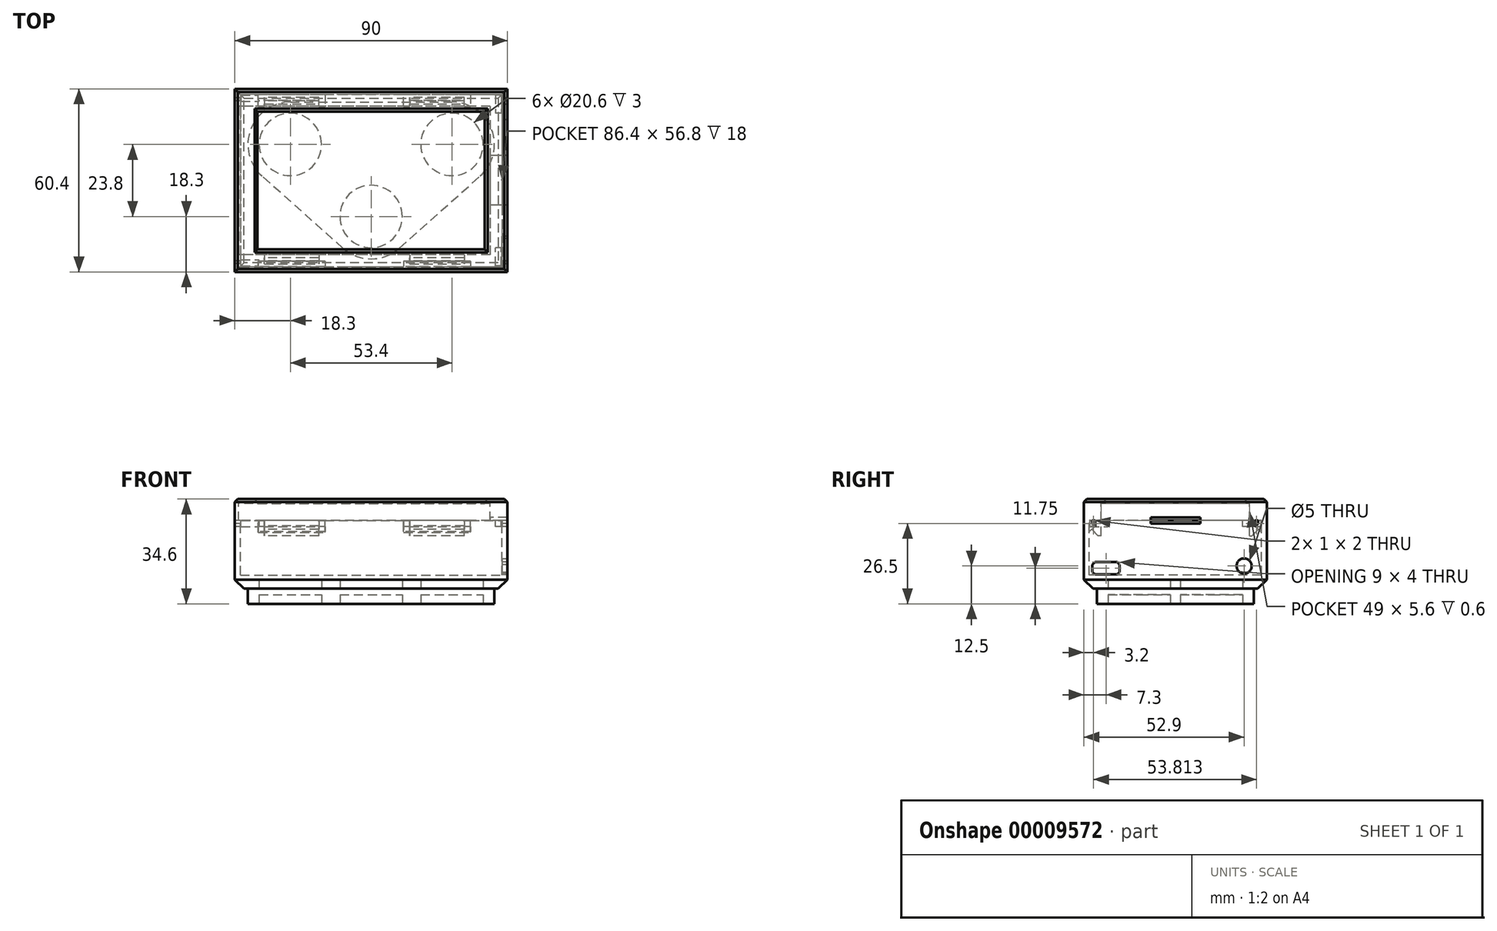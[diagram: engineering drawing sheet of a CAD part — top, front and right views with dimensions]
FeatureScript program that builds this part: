
annotation { "Feature Type Name" : "Feature", "Feature Type Description" : "" }
export const myFeature = defineFeature(function(context is Context, id is Id, definition is map)
    precondition{}
    {
        {
            var Q0;
            Q0=qCreatedBy(makeId("Top.planeOp"),FACE);
            var sketch = newSketch(context, id + "F0", { "sketchPlane" : qUnion([Q0])});
            skLineSegment(sketch, "E0.bottom", {"start": v(-82.5, 48.4) * mm, "end": v(0, 48.4) * mm});
            skLineSegment(sketch, "E0.top", {"start": v(-82.5, 0) * mm, "end": v(0, 0) * mm});
            skLineSegment(sketch, "E0.left", {"start": v(-82.5, 48.4) * mm, "end": v(-82.5, 0) * mm});
            skLineSegment(sketch, "E0.right", {"start": v(0, 48.4) * mm, "end": v(0, 0) * mm});
            skLineSegment(sketch, "E1", {"start": v(-78, 48.4) * mm, "end": v(-78, 0) * mm, "construction": true});
            skLineSegment(sketch, "E2", {"start": v(-78, 48.4) * mm, "end": v(0, 0) * mm, "construction": true});
            skLineSegment(sketch, "E3", {"start": v(0, 48.4) * mm, "end": v(-78, 0) * mm, "construction": true});
            skPoint(sketch, "E4", {"position": v(-39, 24.2) * mm});
            skSolve(sketch);
        }
        {
            var Q0;
            Q0=qCreatedBy(makeId("Top.planeOp"),FACE);
            var sketch = newSketch(context, id + "F1", { "sketchPlane" : qUnion([Q0])});
            skLineSegment(sketch, "E5.bottom", {"start": v(6, 54.4) * mm, "end": v(-84, 54.4) * mm});
            skLineSegment(sketch, "E5.top", {"start": v(6, -6) * mm, "end": v(-84, -6) * mm});
            skLineSegment(sketch, "E5.left", {"start": v(6, 54.4) * mm, "end": v(6, -6) * mm});
            skLineSegment(sketch, "E5.right", {"start": v(-84, 54.4) * mm, "end": v(-84, -6) * mm});
            skPoint(sketch, "E6", {"position": v(-39, 54.4) * mm});
            skPoint(sketch, "E7", {"position": v(6, 24.2) * mm});
            skLineSegment(sketch, "E8.bottom", {"start": v(-76.5, 46.9) * mm, "end": v(-1.5, 46.9) * mm});
            skLineSegment(sketch, "E8.top", {"start": v(-76.5, 1.5) * mm, "end": v(-1.5, 1.5) * mm});
            skLineSegment(sketch, "E8.left", {"start": v(-76.5, 46.9) * mm, "end": v(-76.5, 1.5) * mm});
            skLineSegment(sketch, "E8.right", {"start": v(-1.5, 46.9) * mm, "end": v(-1.5, 1.5) * mm});
            skSolve(sketch);
        }
        {
            var Q0;
            Q0 = qSketchRegion(id + "F1", true);
            extrude(context, id + "F2", {"entities" : qUnion([Q0]), "depth" : 1.5 * mm});
        }
        {
            var Q0;
            Q0=makeQuery(id+"F2.opExtrude","CAP_EDGE",EDGE,{"disambiguationData":[OSD([sQuery(id+"F1.wireOp",EDGE,"E8.bottom")])],"isStart":false});
            var Q1;
            Q1=makeQuery(id+"F2.opExtrude","CAP_EDGE",EDGE,{"disambiguationData":[OSD([sQuery(id+"F1.wireOp",EDGE,"E8.left")])],"isStart":false});
            var Q2;
            Q2=makeQuery(id+"F2.opExtrude","CAP_EDGE",EDGE,{"disambiguationData":[OSD([sQuery(id+"F1.wireOp",EDGE,"E8.top")])],"isStart":false});
            var Q3;
            Q3=makeQuery(id+"F2.opExtrude","CAP_EDGE",EDGE,{"disambiguationData":[OSD([sQuery(id+"F1.wireOp",EDGE,"E8.right")])],"isStart":false});
            var Q4;
            Q4=makeQuery(id+"F2.opExtrude","CAP_EDGE",EDGE,{"disambiguationData":[OSD([sQuery(id+"F1.wireOp",EDGE,"E5.right")])],"isStart":false});
            var Q5;
            Q5=makeQuery(id+"F2.opExtrude","CAP_EDGE",EDGE,{"disambiguationData":[OSD([sQuery(id+"F1.wireOp",EDGE,"E5.top")])],"isStart":false});
            var Q6;
            Q6=makeQuery(id+"F2.opExtrude","CAP_EDGE",EDGE,{"disambiguationData":[OSD([sQuery(id+"F1.wireOp",EDGE,"E5.left")])],"isStart":false});
            var Q7;
            Q7=makeQuery(id+"F2.opExtrude","CAP_EDGE",EDGE,{"disambiguationData":[OSD([sQuery(id+"F1.wireOp",EDGE,"E5.bottom")])],"isStart":false});
            chamfer(context, id + "F3", {"entities" : qUnion([Q0, Q1, Q2, Q3, Q4, Q5, Q6, Q7]), "width" : 1 * mm, "tangentPropagation" : true});
        }
        {
            var Q0;
            Q0=makeQuery(id+"F2.opExtrude","CAP_FACE",FACE,{"disambiguationData":[OSD([sQuery(id+"F1.wireOp",EDGE,"E5.bottom"),sQuery(id+"F1.wireOp",EDGE,"E5.top"),sQuery(id+"F1.wireOp",EDGE,"E5.left"),sQuery(id+"F1.wireOp",EDGE,"E5.right"),sQuery(id+"F1.wireOp",EDGE,"E8.bottom"),sQuery(id+"F1.wireOp",EDGE,"E8.top"),sQuery(id+"F1.wireOp",EDGE,"E8.left"),sQuery(id+"F1.wireOp",EDGE,"E8.right")])],"isStart":true});
            var sketch = newSketch(context, id + "F4", { "sketchPlane" : qUnion([Q0])});
            skLineSegment(sketch, "E9", {"start": v(-84, 6) * mm, "end": v(-84, -54.4) * mm});
            skLineSegment(sketch, "E10", {"start": v(-84, -54.4) * mm, "end": v(6, -54.4) * mm});
            skLineSegment(sketch, "E11", {"start": v(6, -54.4) * mm, "end": v(6, 6) * mm});
            skLineSegment(sketch, "E12", {"start": v(6, 6) * mm, "end": v(-84, 6) * mm});
            skLineSegment(sketch, "E13.bottom", {"start": v(0.3, -48.7) * mm, "end": v(-82.8, -48.7) * mm});
            skLineSegment(sketch, "E13.top", {"start": v(0.3, 0.3) * mm, "end": v(-82.8, 0.3) * mm});
            skLineSegment(sketch, "E13.left", {"start": v(0.3, -48.7) * mm, "end": v(0.3, 0.3) * mm});
            skLineSegment(sketch, "E13.right", {"start": v(-82.8, -48.7) * mm, "end": v(-82.8, 0.3) * mm});
            skSolve(sketch);
        }
        {
            var Q0;
            Q0 = qSketchRegion(id + "F4", true);
            extrude(context, id + "F5", {"entities" : qUnion([Q0]), "operationType" : NewBodyOperationType.ADD, "depth" : 5.6 * mm});
        }
        {
            var Q0;
            Q0=makeQuery(id+"F5.opExtrude","CAP_FACE",FACE,{"disambiguationData":[OSD([sQuery(id+"F4.wireOp",EDGE,"E9"),sQuery(id+"F4.wireOp",EDGE,"E10"),sQuery(id+"F4.wireOp",EDGE,"E11"),sQuery(id+"F4.wireOp",EDGE,"E12"),sQuery(id+"F4.wireOp",EDGE,"E13.bottom"),sQuery(id+"F4.wireOp",EDGE,"E13.top"),sQuery(id+"F4.wireOp",EDGE,"E13.left"),sQuery(id+"F4.wireOp",EDGE,"E13.right")])],"isStart":false});
            var sketch = newSketch(context, id + "F6", { "sketchPlane" : qUnion([Q0])});
            skLineSegment(sketch, "E14.bottom", {"start": v(6, -16) * mm, "end": v(0.3, -16) * mm});
            skLineSegment(sketch, "E14.top", {"start": v(6, -32.4) * mm, "end": v(0.3, -32.4) * mm});
            skLineSegment(sketch, "E14.left", {"start": v(6, -16) * mm, "end": v(6, -32.4) * mm});
            skLineSegment(sketch, "E14.right", {"start": v(0.3, -16) * mm, "end": v(0.3, -32.4) * mm});
            skSolve(sketch);
        }
        {
            var Q0;
            Q0 = qSketchRegion(id + "F6", true);
            extrude(context, id + "F7", {"entities" : qUnion([Q0]), "operationType" : NewBodyOperationType.REMOVE, "oppositeDirection" : true, "depth" : 0.4 * mm});
        }
        {
            var Q0;
            Q0=makeQuery(id+"F5.opExtrude","CAP_FACE",FACE,{"disambiguationData":[OSD([sQuery(id+"F4.wireOp",EDGE,"E9"),sQuery(id+"F4.wireOp",EDGE,"E10"),sQuery(id+"F4.wireOp",EDGE,"E11"),sQuery(id+"F4.wireOp",EDGE,"E12"),sQuery(id+"F4.wireOp",EDGE,"E13.bottom"),sQuery(id+"F4.wireOp",EDGE,"E13.top"),sQuery(id+"F4.wireOp",EDGE,"E13.left"),sQuery(id+"F4.wireOp",EDGE,"E13.right")])],"isStart":false});
            var sketch = newSketch(context, id + "F8", { "sketchPlane" : qUnion([Q0])});
            skLineSegment(sketch, "E15", {"start": v(-84, 6) * mm, "end": v(-84, -54.4) * mm});
            skLineSegment(sketch, "E16", {"start": v(-84, -54.4) * mm, "end": v(6, -54.4) * mm});
            skLineSegment(sketch, "E17", {"start": v(6, -54.4) * mm, "end": v(6, 6) * mm});
            skLineSegment(sketch, "E18", {"start": v(6, 6) * mm, "end": v(-84, 6) * mm});
            skSolve(sketch);
        }
        {
            var Q0;
            Q0 = qSketchRegion(id + "F8", true);
            extrude(context, id + "F9", {"entities" : qUnion([Q0]), "depth" : 22.5 * mm});
        }
        {
            var Q0;
            Q0=makeQuery(id+"F9.opExtrude","CAP_FACE",FACE,{"disambiguationData":[OSD([sQuery(id+"F8.wireOp",EDGE,"E15"),sQuery(id+"F8.wireOp",EDGE,"E16"),sQuery(id+"F8.wireOp",EDGE,"E17"),sQuery(id+"F8.wireOp",EDGE,"E18")])],"isStart":true});
            var sketch = newSketch(context, id + "F10", { "sketchPlane" : qUnion([Q0])});
            skLineSegment(sketch, "E19.bottom", {"start": v(6, 32.4) * mm, "end": v(0.3, 32.4) * mm});
            skLineSegment(sketch, "E19.top", {"start": v(6, 16) * mm, "end": v(0.3, 16) * mm});
            skLineSegment(sketch, "E19.left", {"start": v(6, 32.4) * mm, "end": v(6, 16) * mm});
            skLineSegment(sketch, "E19.right", {"start": v(0.3, 32.4) * mm, "end": v(0.3, 16) * mm});
            skSolve(sketch);
        }
        {
            var Q0;
            Q0 = qSketchRegion(id + "F10", true);
            extrude(context, id + "F11", {"entities" : qUnion([Q0]), "operationType" : NewBodyOperationType.REMOVE, "endBound" : BoundingType.SYMMETRIC, "oppositeDirection" : true, "depth" : 2 * mm});
        }
        {
            var Q0;
            Q0=makeQuery(id+"F9.opExtrude","SWEPT_FACE",FACE,{"disambiguationData":[OSD([sQuery(id+"F8.wireOp",EDGE,"E17")])]});
            var sketch = newSketch(context, id + "F12", { "sketchPlane" : qUnion([Q0])});
            skCircle(sketch, "E20", {"center": v(46.9, -20.6) * mm, "radius": 2.5 * mm});
            skSolve(sketch);
        }
        {
            var Q0;
            Q0 = qSketchRegion(id + "F12", true);
            extrude(context, id + "F13", {"entities" : qUnion([Q0]), "operationType" : NewBodyOperationType.REMOVE, "oppositeDirection" : true, "depth" : 20 * mm});
        }
        {
            var Q0;
            Q0=makeQuery(id+"F9.opExtrude","CAP_FACE",FACE,{"disambiguationData":[OSD([sQuery(id+"F8.wireOp",EDGE,"E15"),sQuery(id+"F8.wireOp",EDGE,"E16"),sQuery(id+"F8.wireOp",EDGE,"E17"),sQuery(id+"F8.wireOp",EDGE,"E18")])],"isStart":true});
            var sketch = newSketch(context, id + "F14", { "sketchPlane" : qUnion([Q0])});
            skLineSegment(sketch, "E21.bottom", {"start": v(-82.2, 52.6) * mm, "end": v(4.2, 52.6) * mm});
            skLineSegment(sketch, "E21.top", {"start": v(-82.2, -4.2) * mm, "end": v(4.2, -4.2) * mm});
            skLineSegment(sketch, "E21.left", {"start": v(-82.2, 52.6) * mm, "end": v(-82.2, -4.2) * mm});
            skLineSegment(sketch, "E21.right", {"start": v(4.2, 52.6) * mm, "end": v(4.2, -4.2) * mm});
            skSolve(sketch);
        }
        {
            var Q0;
            Q0 = qSketchRegion(id + "F14", true);
            extrude(context, id + "F15", {"entities" : qUnion([Q0]), "operationType" : NewBodyOperationType.REMOVE, "oppositeDirection" : true, "depth" : 18 * mm});
        }
        {
            var Q0;
            Q0=makeQuery(id+"F15.boolean.opBoolean","COPY",FACE,{"derivedFrom":makeQuery(id+"F15.opExtrude","SWEPT_FACE",FACE,{"disambiguationData":[OSD([sQuery(id+"F14.wireOp",EDGE,"E21.right")])]})});
            var sketch = newSketch(context, id + "F16", { "sketchPlane" : qUnion([Q0])});
            skLineSegment(sketch, "E22.bottom", {"start": v(3.2, -19.35) * mm, "end": v(-5.8, -19.35) * mm});
            skLineSegment(sketch, "E22.top", {"start": v(3.2, -23.35) * mm, "end": v(-5.8, -23.35) * mm});
            skLineSegment(sketch, "E22.left", {"start": v(3.2, -19.35) * mm, "end": v(3.2, -23.35) * mm});
            skLineSegment(sketch, "E22.right", {"start": v(-5.8, -19.35) * mm, "end": v(-5.8, -23.35) * mm});
            skPoint(sketch, "E23", {"position": v(-1.3, -19.35) * mm});
            skPoint(sketch, "E24", {"position": v(-5.8, -21.35) * mm});
            skSolve(sketch);
        }
        {
            var Q0;
            Q0 = qSketchRegion(id + "F16", true);
            var Q1;
            Q1=makeQuery(id+"F9.opExtrude","SWEPT_FACE",FACE,{"disambiguationData":[OSD([sQuery(id+"F8.wireOp",EDGE,"E17")])]});
            extrude(context, id + "F17", {"entities" : qUnion([Q0]), "operationType" : NewBodyOperationType.REMOVE, "endBound" : BoundingType.UP_TO_SURFACE, "oppositeDirection" : true, "endBoundEntityFace" : qUnion([Q1]), "depth" : 25 * mm});
        }
        {
            var Q0;
            Q0=makeQuery(id+"F17.boolean.opBoolean","COPY",EDGE,{"derivedFrom":makeQuery(id+"F17.opExtrude","SWEPT_EDGE",EDGE,{"disambiguationData":[OSD([sQuery(id+"F16.wireOp",EDGE,"E22.top"),sQuery(id+"F16.wireOp",EDGE,"E22.left")])]})});
            var Q1;
            Q1=makeQuery(id+"F17.boolean.opBoolean","COPY",EDGE,{"derivedFrom":makeQuery(id+"F17.opExtrude","SWEPT_EDGE",EDGE,{"disambiguationData":[OSD([sQuery(id+"F16.wireOp",EDGE,"E22.bottom"),sQuery(id+"F16.wireOp",EDGE,"E22.left")])]})});
            var Q2;
            Q2=makeQuery(id+"F17.boolean.opBoolean","COPY",EDGE,{"derivedFrom":makeQuery(id+"F17.opExtrude","SWEPT_EDGE",EDGE,{"disambiguationData":[OSD([sQuery(id+"F16.wireOp",EDGE,"E22.bottom"),sQuery(id+"F16.wireOp",EDGE,"E22.right")])]})});
            var Q3;
            Q3=makeQuery(id+"F17.boolean.opBoolean","COPY",EDGE,{"derivedFrom":makeQuery(id+"F17.opExtrude","SWEPT_EDGE",EDGE,{"disambiguationData":[OSD([sQuery(id+"F16.wireOp",EDGE,"E22.top"),sQuery(id+"F16.wireOp",EDGE,"E22.right")])]})});
            chamfer(context, id + "F18", {"entities" : qUnion([Q0, Q1, Q2, Q3]), "width" : 0.8 * mm, "tangentPropagation" : true});
        }
        {
            var Q0;
            Q0=makeQuery(id+"F9.opExtrude","CAP_FACE",FACE,{"disambiguationData":[OSD([sQuery(id+"F8.wireOp",EDGE,"E15"),sQuery(id+"F8.wireOp",EDGE,"E16"),sQuery(id+"F8.wireOp",EDGE,"E17"),sQuery(id+"F8.wireOp",EDGE,"E18")])],"isStart":false});
            var sketch = newSketch(context, id + "F19", { "sketchPlane" : qUnion([Q0])});
            skCircle(sketch, "E25", {"center": v(-12.3, -36.1) * mm, "radius": 10.3 * mm});
            skCircle(sketch, "E26", {"center": v(-65.7, -36.1) * mm, "radius": 10.3 * mm});
            skCircle(sketch, "E27", {"center": v(-39, -12.3) * mm, "radius": 10.3 * mm});
            skLineSegment(sketch, "E28", {"start": v(-12.3, -46.4) * mm, "end": v(-65.7, -46.4) * mm, "construction": true});
            skLineSegment(sketch, "E29", {"start": v(-72.55, -28.41) * mm, "end": v(-45.85, -4.61) * mm, "construction": true});
            skLineSegment(sketch, "E30", {"start": v(-32.15, -4.61) * mm, "end": v(-5.45, -28.41) * mm, "construction": true});
            skPoint(sketch, "E31", {"position": v(-39, -46.4) * mm});
            skPoint(sketch, "E32", {"position": v(-39, -54.4) * mm});
            skSolve(sketch);
        }
        {
            var Q0;
            Q0 = qSketchRegion(id + "F19", true);
            extrude(context, id + "F20", {"entities" : qUnion([Q0]), "operationType" : NewBodyOperationType.REMOVE, "oppositeDirection" : true, "depth" : 3 * mm});
        }
        {
            var Q0;
            Q0=makeQuery(id+"F9.opExtrude","CAP_EDGE",EDGE,{"disambiguationData":[OSD([sQuery(id+"F8.wireOp",EDGE,"E17")])],"isStart":false});
            var Q1;
            Q1=makeQuery(id+"F9.opExtrude","CAP_EDGE",EDGE,{"disambiguationData":[OSD([sQuery(id+"F8.wireOp",EDGE,"E16")])],"isStart":false});
            var Q2;
            Q2=makeQuery(id+"F9.opExtrude","CAP_EDGE",EDGE,{"disambiguationData":[OSD([sQuery(id+"F8.wireOp",EDGE,"E15")])],"isStart":false});
            var Q3;
            Q3=makeQuery(id+"F9.opExtrude","CAP_EDGE",EDGE,{"disambiguationData":[OSD([sQuery(id+"F8.wireOp",EDGE,"E18")])],"isStart":false});
            chamfer(context, id + "F21", {"entities" : qUnion([Q0, Q1, Q2, Q3]), "width" : 3 * mm, "tangentPropagation" : true});
        }
        {
            var Q0;
            Q0=makeQuery(id+"F5.opExtrude","CAP_FACE",FACE,{"disambiguationData":[OSD([sQuery(id+"F4.wireOp",EDGE,"E9"),sQuery(id+"F4.wireOp",EDGE,"E10"),sQuery(id+"F4.wireOp",EDGE,"E11"),sQuery(id+"F4.wireOp",EDGE,"E12"),sQuery(id+"F4.wireOp",EDGE,"E13.bottom"),sQuery(id+"F4.wireOp",EDGE,"E13.top"),sQuery(id+"F4.wireOp",EDGE,"E13.left"),sQuery(id+"F4.wireOp",EDGE,"E13.right")])],"isStart":false});
            var sketch = newSketch(context, id + "F22", { "sketchPlane" : qUnion([Q0])});
            skLineSegment(sketch, "E33.bottom", {"start": v(-74.25, 0.3) * mm, "end": v(-56.25, 0.3) * mm});
            skLineSegment(sketch, "E33.top", {"start": v(-74.25, 3.3) * mm, "end": v(-56.25, 3.3) * mm});
            skLineSegment(sketch, "E33.left", {"start": v(-74.25, 0.3) * mm, "end": v(-74.25, 3.3) * mm});
            skLineSegment(sketch, "E33.right", {"start": v(-56.25, 0.3) * mm, "end": v(-56.25, 3.3) * mm});
            skLineSegment(sketch, "E34.bottom", {"start": v(-26.25, 0.3) * mm, "end": v(-8.25, 0.3) * mm});
            skLineSegment(sketch, "E34.top", {"start": v(-26.25, 3.3) * mm, "end": v(-8.25, 3.3) * mm});
            skLineSegment(sketch, "E34.left", {"start": v(-26.25, 0.3) * mm, "end": v(-26.25, 3.3) * mm});
            skLineSegment(sketch, "E34.right", {"start": v(-8.25, 0.3) * mm, "end": v(-8.25, 3.3) * mm});
            skLineSegment(sketch, "E35.bottom", {"start": v(-74.25, -48.7) * mm, "end": v(-56.25, -48.7) * mm});
            skLineSegment(sketch, "E35.top", {"start": v(-74.25, -51.51) * mm, "end": v(-56.25, -51.51) * mm});
            skLineSegment(sketch, "E35.left", {"start": v(-74.25, -48.7) * mm, "end": v(-74.25, -51.51) * mm});
            skLineSegment(sketch, "E35.right", {"start": v(-56.25, -48.7) * mm, "end": v(-56.25, -51.51) * mm});
            skLineSegment(sketch, "E36.bottom", {"start": v(-26.25, -48.7) * mm, "end": v(-8.25, -48.7) * mm});
            skLineSegment(sketch, "E36.top", {"start": v(-26.25, -51.51) * mm, "end": v(-8.25, -51.51) * mm});
            skLineSegment(sketch, "E36.left", {"start": v(-26.25, -48.7) * mm, "end": v(-26.25, -51.51) * mm});
            skLineSegment(sketch, "E36.right", {"start": v(-8.25, -48.7) * mm, "end": v(-8.25, -51.51) * mm});
            skPoint(sketch, "E37", {"position": v(-41.25, 0.3) * mm});
            skSolve(sketch);
        }
        {
            var Q0;
            Q0 = qSketchRegion(id + "F22", true);
            extrude(context, id + "F23", {"entities" : qUnion([Q0]), "operationType" : NewBodyOperationType.ADD, "depth" : 5 * mm});
        }
        {
            var Q0;
            Q0=makeQuery(id+"F5.boolean.opBoolean","MERGE",FACE,{"derivedFrom":[makeQuery(id+"F2.opExtrude","SWEPT_FACE",FACE,{"disambiguationData":[OSD([sQuery(id+"F1.wireOp",EDGE,"E5.right")])]}),makeQuery(id+"F5.opExtrude","SWEPT_FACE",FACE,{"disambiguationData":[OSD([sQuery(id+"F4.wireOp",EDGE,"E9")])]})]});
            var sketch = newSketch(context, id + "F24", { "sketchPlane" : qUnion([Q0])});
            skLineSegment(sketch, "E38.bottom", {"start": v(-51.51, -5.6) * mm, "end": v(-50.51, -5.6) * mm});
            skLineSegment(sketch, "E38.top", {"start": v(-51.51, -7.6) * mm, "end": v(-50.51, -7.6) * mm});
            skLineSegment(sketch, "E38.left", {"start": v(-51.51, -5.6) * mm, "end": v(-51.51, -7.6) * mm});
            skLineSegment(sketch, "E38.right", {"start": v(-50.51, -5.6) * mm, "end": v(-50.51, -7.6) * mm});
            skLineSegment(sketch, "E39.bottom", {"start": v(3.3, -5.6) * mm, "end": v(2.3, -5.6) * mm});
            skLineSegment(sketch, "E39.top", {"start": v(3.3, -7.6) * mm, "end": v(2.3, -7.6) * mm});
            skLineSegment(sketch, "E39.left", {"start": v(3.3, -5.6) * mm, "end": v(3.3, -7.6) * mm});
            skLineSegment(sketch, "E39.right", {"start": v(2.3, -5.6) * mm, "end": v(2.3, -7.6) * mm});
            skSolve(sketch);
        }
        {
            var Q0;
            Q0 = qSketchRegion(id + "F24", true);
            extrude(context, id + "F25", {"entities" : qUnion([Q0]), "operationType" : NewBodyOperationType.REMOVE, "endBound" : BoundingType.THROUGH_ALL, "oppositeDirection" : true, "depth" : 25 * mm});
        }
        {
            var Q0;
            Q0=makeQuery(id+"F23.opExtrude","CAP_EDGE",EDGE,{"disambiguationData":[OSD([sQuery(id+"F22.wireOp",EDGE,"E36.top")])],"isStart":false});
            var Q1;
            Q1=makeQuery(id+"F23.opExtrude","CAP_EDGE",EDGE,{"disambiguationData":[OSD([sQuery(id+"F22.wireOp",EDGE,"E35.top")])],"isStart":false});
            var Q2;
            Q2=makeQuery(id+"F23.opExtrude","CAP_EDGE",EDGE,{"disambiguationData":[OSD([sQuery(id+"F22.wireOp",EDGE,"E33.top")])],"isStart":false});
            var Q3;
            Q3=makeQuery(id+"F23.opExtrude","CAP_EDGE",EDGE,{"disambiguationData":[OSD([sQuery(id+"F22.wireOp",EDGE,"E34.top")])],"isStart":false});
            chamfer(context, id + "F26", {"entities" : qUnion([Q0, Q1, Q2, Q3]), "width" : 2 * mm, "tangentPropagation" : true});
        }
        {
            var Q0;
            Q0=makeQuery(id+"F25.boolean.opBoolean","COPY",EDGE,{"disambiguationData":[OD(1.0)],"derivedFrom":makeQuery(id+"F25.opExtrude","SWEPT_EDGE",EDGE,{"disambiguationData":[OSD([sQuery(id+"F24.wireOp",EDGE,"E39.top"),sQuery(id+"F24.wireOp",EDGE,"E39.left")])]})});
            var Q1;
            Q1=makeQuery(id+"F25.boolean.opBoolean","COPY",EDGE,{"disambiguationData":[OD(0.0)],"derivedFrom":makeQuery(id+"F25.opExtrude","SWEPT_EDGE",EDGE,{"disambiguationData":[OSD([sQuery(id+"F24.wireOp",EDGE,"E39.top"),sQuery(id+"F24.wireOp",EDGE,"E39.left")])]})});
            var Q2;
            Q2=makeQuery(id+"F25.boolean.opBoolean","COPY",EDGE,{"disambiguationData":[OD(1.0)],"derivedFrom":makeQuery(id+"F25.opExtrude","SWEPT_EDGE",EDGE,{"disambiguationData":[OSD([sQuery(id+"F24.wireOp",EDGE,"E38.top"),sQuery(id+"F24.wireOp",EDGE,"E38.left")])]})});
            var Q3;
            Q3=makeQuery(id+"F25.boolean.opBoolean","COPY",EDGE,{"disambiguationData":[OD(0.0)],"derivedFrom":makeQuery(id+"F25.opExtrude","SWEPT_EDGE",EDGE,{"disambiguationData":[OSD([sQuery(id+"F24.wireOp",EDGE,"E38.top"),sQuery(id+"F24.wireOp",EDGE,"E38.left")])]})});
            chamfer(context, id + "F27", {"entities" : qUnion([Q0, Q1, Q2, Q3]), "width" : 1 * mm, "tangentPropagation" : true});
        }
        {
            var Q0;
            Q0=makeQuery(id+"F22.imprint","IMPRINT",FACE,{"disambiguationData":[TD([[makeQuery(id+"F22.imprint","IMPRINT",EDGE,{"derivedFrom":sQuery(id+"F22.wireOp",EDGE,"E33.top")}),1.0]])]});
            var sketch = newSketch(context, id + "F28", { "sketchPlane" : qUnion([Q0])});
            skLineSegment(sketch, "E40.bottom", {"start": v(-76.25, -52.6) * mm, "end": v(-54.25, -52.6) * mm});
            skLineSegment(sketch, "E40.top", {"start": v(-76.25, -50.71) * mm, "end": v(-54.25, -50.71) * mm});
            skLineSegment(sketch, "E40.left", {"start": v(-76.25, -50.71) * mm, "end": v(-76.25, -52.6) * mm});
            skLineSegment(sketch, "E40.right", {"start": v(-54.25, -50.71) * mm, "end": v(-54.25, -52.6) * mm});
            skLineSegment(sketch, "E41.bottom", {"start": v(-28.25, -52.6) * mm, "end": v(-6.25, -52.6) * mm});
            skLineSegment(sketch, "E41.top", {"start": v(-28.25, -50.71) * mm, "end": v(-6.25, -50.71) * mm});
            skLineSegment(sketch, "E41.left", {"start": v(-28.25, -50.71) * mm, "end": v(-28.25, -52.6) * mm});
            skLineSegment(sketch, "E41.right", {"start": v(-6.25, -50.71) * mm, "end": v(-6.25, -52.6) * mm});
            skLineSegment(sketch, "E42.bottom", {"start": v(-6.25, 2.5) * mm, "end": v(-28.25, 2.5) * mm});
            skLineSegment(sketch, "E42.top", {"start": v(-6.25, 4.2) * mm, "end": v(-28.25, 4.2) * mm});
            skLineSegment(sketch, "E42.left", {"start": v(-6.25, 2.5) * mm, "end": v(-6.25, 4.2) * mm});
            skLineSegment(sketch, "E42.right", {"start": v(-28.25, 2.5) * mm, "end": v(-28.25, 4.2) * mm});
            skLineSegment(sketch, "E43.bottom", {"start": v(-54.25, 2.5) * mm, "end": v(-76.25, 2.5) * mm});
            skLineSegment(sketch, "E43.top", {"start": v(-54.25, 4.2) * mm, "end": v(-76.25, 4.2) * mm});
            skLineSegment(sketch, "E43.left", {"start": v(-54.25, 2.5) * mm, "end": v(-54.25, 4.2) * mm});
            skLineSegment(sketch, "E43.right", {"start": v(-76.25, 2.5) * mm, "end": v(-76.25, 4.2) * mm});
            skPoint(sketch, "E44", {"position": v(-39, -54.4) * mm});
            skPoint(sketch, "E45", {"position": v(-65.25, -50.71) * mm});
            skPoint(sketch, "E46", {"position": v(-65.25, -48.7) * mm});
            skPoint(sketch, "E47", {"position": v(-17.25, -48.7) * mm});
            skPoint(sketch, "E48", {"position": v(-17.25, -50.71) * mm});
            skSolve(sketch);
        }
        {
            var Q0;
            Q0 = qSketchRegion(id + "F28", true);
            extrude(context, id + "F29", {"entities" : qUnion([Q0]), "operationType" : NewBodyOperationType.ADD, "depth" : 4 * mm});
        }
        {
            var Q0;
            Q0=makeQuery(id+"F29.opExtrude","CAP_EDGE",EDGE,{"disambiguationData":[OSD([sQuery(id+"F28.wireOp",EDGE,"E41.top")])],"isStart":false});
            var Q1;
            Q1=makeQuery(id+"F29.opExtrude","CAP_EDGE",EDGE,{"disambiguationData":[OSD([sQuery(id+"F28.wireOp",EDGE,"E40.top")])],"isStart":false});
            var Q2;
            Q2=makeQuery(id+"F29.opExtrude","CAP_EDGE",EDGE,{"disambiguationData":[OSD([sQuery(id+"F28.wireOp",EDGE,"E42.bottom")])],"isStart":false});
            var Q3;
            Q3=makeQuery(id+"F29.opExtrude","CAP_EDGE",EDGE,{"disambiguationData":[OSD([sQuery(id+"F28.wireOp",EDGE,"E43.bottom")])],"isStart":false});
            var Q4;
            Q4=makeQuery(id+"F29.opExtrude","CAP_EDGE",EDGE,{"disambiguationData":[OSD([sQuery(id+"F28.wireOp",EDGE,"E40.top")])],"isStart":true});
            var Q5;
            Q5=makeQuery(id+"F29.opExtrude","CAP_EDGE",EDGE,{"disambiguationData":[OSD([sQuery(id+"F28.wireOp",EDGE,"E41.top")])],"isStart":true});
            var Q6;
            Q6=makeQuery(id+"F29.opExtrude","CAP_EDGE",EDGE,{"disambiguationData":[OSD([sQuery(id+"F28.wireOp",EDGE,"E42.bottom")])],"isStart":true});
            chamfer(context, id + "F30", {"entities" : qUnion([Q0, Q1, Q2, Q3, Q4, Q5, Q6]), "width" : 2 * mm, "tangentPropagation" : true});
        }
        {
            var Q0;
            Q0=makeQuery(id+"F22.imprint","IMPRINT",FACE,{"disambiguationData":[TD([[makeQuery(id+"F22.imprint","IMPRINT",EDGE,{"derivedFrom":sQuery(id+"F22.wireOp",EDGE,"E33.top")}),1.0]])]});
            var sketch = newSketch(context, id + "F31", { "sketchPlane" : qUnion([Q0])});
            skLineSegment(sketch, "E49.bottom", {"start": v(4, 4) * mm, "end": v(2, 4) * mm});
            skLineSegment(sketch, "E49.top", {"start": v(4, -2) * mm, "end": v(2, -2) * mm});
            skLineSegment(sketch, "E49.left", {"start": v(4, 4) * mm, "end": v(4, -2) * mm});
            skLineSegment(sketch, "E49.right", {"start": v(2, 4) * mm, "end": v(2, -2) * mm});
            skLineSegment(sketch, "E50.bottom", {"start": v(4, -52.4) * mm, "end": v(2, -52.4) * mm});
            skLineSegment(sketch, "E50.top", {"start": v(4, -46.4) * mm, "end": v(2, -46.4) * mm});
            skLineSegment(sketch, "E50.left", {"start": v(4, -52.4) * mm, "end": v(4, -46.4) * mm});
            skLineSegment(sketch, "E50.right", {"start": v(2, -52.4) * mm, "end": v(2, -46.4) * mm});
            skLineSegment(sketch, "E51.bottom", {"start": v(-82, 4) * mm, "end": v(-76, 4) * mm});
            skLineSegment(sketch, "E51.top", {"start": v(-82, 2) * mm, "end": v(-76, 2) * mm});
            skLineSegment(sketch, "E51.left", {"start": v(-82, 4) * mm, "end": v(-82, 2) * mm});
            skLineSegment(sketch, "E51.right", {"start": v(-76, 4) * mm, "end": v(-76, 2) * mm});
            skLineSegment(sketch, "E52.bottom", {"start": v(-82, -52.4) * mm, "end": v(-76, -52.4) * mm});
            skLineSegment(sketch, "E52.top", {"start": v(-82, -50.4) * mm, "end": v(-76, -50.4) * mm});
            skLineSegment(sketch, "E52.left", {"start": v(-82, -52.4) * mm, "end": v(-82, -50.4) * mm});
            skLineSegment(sketch, "E52.right", {"start": v(-76, -52.4) * mm, "end": v(-76, -50.4) * mm});
            skSolve(sketch);
        }
        {
            var Q0;
            Q0 = qSketchRegion(id + "F31", true);
            extrude(context, id + "F32", {"entities" : qUnion([Q0]), "operationType" : NewBodyOperationType.ADD, "depth" : 2 * mm});
        }
        {
            var Q0;
            Q0=makeQuery(id+"F9.opExtrude","CAP_FACE",FACE,{"disambiguationData":[OSD([sQuery(id+"F8.wireOp",EDGE,"E15"),sQuery(id+"F8.wireOp",EDGE,"E16"),sQuery(id+"F8.wireOp",EDGE,"E17"),sQuery(id+"F8.wireOp",EDGE,"E18")])],"isStart":false});
            var sketch = newSketch(context, id + "F33", { "sketchPlane" : qUnion([Q0])});
            skCircle(sketch, "E53", {"center": v(-39, -12.3) * mm, "radius": 14 * mm});
            skCircle(sketch, "E54", {"center": v(-12.3, -36.1) * mm, "radius": 14 * mm});
            skCircle(sketch, "E55", {"center": v(-65.7, -36.1) * mm, "radius": 14 * mm});
            skLineSegment(sketch, "E56", {"start": v(-65.7, -50.1) * mm, "end": v(-12.3, -50.1) * mm});
            skLineSegment(sketch, "E57", {"start": v(-29.68, -1.85) * mm, "end": v(-2.98, -25.65) * mm});
            skLineSegment(sketch, "E58", {"start": v(-48.32, -1.85) * mm, "end": v(-75.02, -25.65) * mm});
            skSolve(sketch);
        }
        {
            var Q0;
            Q0 = qSketchRegion(id + "F33", true);
            extrude(context, id + "F34", {"entities" : qUnion([Q0]), "depth" : 5 * mm});
        }
        {
            var Q0;
            Q0=makeQuery(id+"F34.opExtrude","CAP_FACE",FACE,{"disambiguationData":[OSD([sQuery(id+"F33.wireOp",EDGE,"E53"),sQuery(id+"F33.wireOp",EDGE,"E54"),sQuery(id+"F33.wireOp",EDGE,"E55"),sQuery(id+"F33.wireOp",EDGE,"E56"),sQuery(id+"F33.wireOp",EDGE,"E57"),sQuery(id+"F33.wireOp",EDGE,"E58")])],"isStart":false});
            var sketch = newSketch(context, id + "F35", { "sketchPlane" : qUnion([Q0])});
            skCircle(sketch, "E59", {"center": v(-39, -12.3) * mm, "radius": 10.3 * mm});
            skCircle(sketch, "E60", {"center": v(-12.3, -36.1) * mm, "radius": 10.3 * mm});
            skCircle(sketch, "E61", {"center": v(-65.7, -36.1) * mm, "radius": 10.3 * mm});
            skSolve(sketch);
        }
        {
            var Q0;
            Q0 = qSketchRegion(id + "F35", true);
            extrude(context, id + "F36", {"entities" : qUnion([Q0]), "operationType" : NewBodyOperationType.REMOVE, "oppositeDirection" : true, "depth" : 3 * mm});
        }
    });
